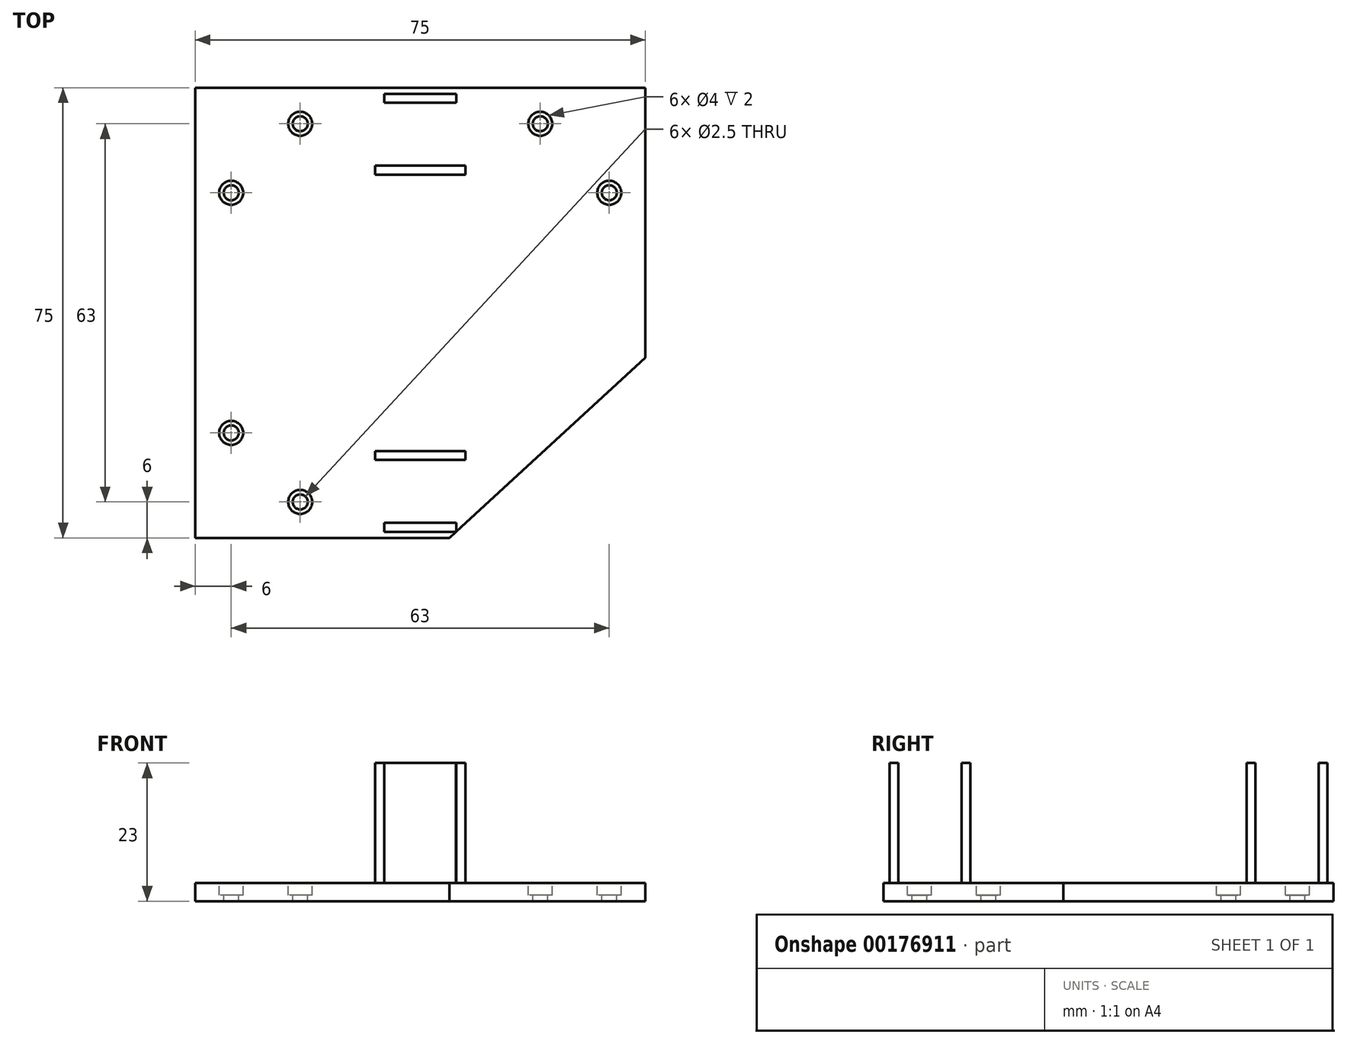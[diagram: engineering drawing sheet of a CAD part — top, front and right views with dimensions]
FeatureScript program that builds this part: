
annotation { "Feature Type Name" : "Feature", "Feature Type Description" : "" }
export const myFeature = defineFeature(function(context is Context, id is Id, definition is map)
    precondition{}
    {
        {
            var Q0;
            Q0=qCreatedBy(makeId("Top.planeOp"),FACE);
            var sketch = newSketch(context, id + "F0", { "sketchPlane" : qUnion([Q0])});
            skLineSegment(sketch, "E0.bottom", {"start": v(-37.5, 37.5) * mm, "end": v(37.5, 37.5) * mm});
            skLineSegment(sketch, "E0.top", {"start": v(-37.5, -37.5) * mm, "end": v(37.5, -37.5) * mm});
            skLineSegment(sketch, "E0.left", {"start": v(-37.5, 37.5) * mm, "end": v(-37.5, -37.5) * mm});
            skLineSegment(sketch, "E0.right", {"start": v(37.5, 37.5) * mm, "end": v(37.5, -37.5) * mm});
            skSolve(sketch);
        }
        {
            var Q0;
            Q0=makeQuery(id+"F0.imprint","IMPRINT",FACE,{"disambiguationData":[TD([[makeQuery(id+"F0.imprint","IMPRINT",EDGE,{"derivedFrom":sQuery(id+"F0.wireOp",EDGE,"E0.bottom")}),-1.0]])]});
            extrude(context, id + "F1", {"entities" : qUnion([Q0]), "depth" : 3 * mm});
        }
        {
            var Q0;
            Q0=makeQuery(id+"F1.opExtrude","CAP_FACE",FACE,{"disambiguationData":[OSD([sQuery(id+"F0.wireOp",EDGE,"E0.bottom"),sQuery(id+"F0.wireOp",EDGE,"E0.top"),sQuery(id+"F0.wireOp",EDGE,"E0.left"),sQuery(id+"F0.wireOp",EDGE,"E0.right")])],"isStart":false});
            var sketch = newSketch(context, id + "F2", { "sketchPlane" : qUnion([Q0])});
            skCircle(sketch, "E1", {"center": v(31.5, -20) * mm, "radius": 2 * mm});
            skCircle(sketch, "E2", {"center": v(20, -31.5) * mm, "radius": 2 * mm});
            skCircle(sketch, "E3", {"center": v(31.5, 20) * mm, "radius": 2 * mm});
            skCircle(sketch, "E4", {"center": v(20, 31.5) * mm, "radius": 2 * mm});
            skCircle(sketch, "E5", {"center": v(-20, 31.5) * mm, "radius": 2 * mm});
            skCircle(sketch, "E6", {"center": v(-31.5, 20) * mm, "radius": 2 * mm});
            skCircle(sketch, "E7", {"center": v(-20, -31.5) * mm, "radius": 2 * mm});
            skCircle(sketch, "E8", {"center": v(-31.5, -20) * mm, "radius": 2 * mm});
            skSolve(sketch);
        }
        {
            var Q0;
            Q0 = qSketchRegion(id + "F2", true);
            extrude(context, id + "F3", {"entities" : qUnion([Q0]), "operationType" : NewBodyOperationType.REMOVE, "oppositeDirection" : true, "depth" : 2 * mm});
        }
        {
            var Q0;
            Q0=makeQuery(id+"F3.boolean.opBoolean","COPY",FACE,{"derivedFrom":makeQuery(id+"F3.opExtrude","CAP_FACE",FACE,{"disambiguationData":[OSD([sQuery(id+"F2.wireOp",EDGE,"E8")])],"isStart":false})});
            var sketch = newSketch(context, id + "F4", { "sketchPlane" : qUnion([Q0])});
            skCircle(sketch, "E9", {"center": v(-31.5, 20) * mm, "radius": 1.25 * mm});
            skCircle(sketch, "E10", {"center": v(-20, 31.5) * mm, "radius": 1.25 * mm});
            skCircle(sketch, "E11", {"center": v(20, 31.5) * mm, "radius": 1.25 * mm});
            skCircle(sketch, "E12", {"center": v(31.5, 20) * mm, "radius": 1.25 * mm});
            skCircle(sketch, "E13", {"center": v(-31.5, -20) * mm, "radius": 1.25 * mm});
            skCircle(sketch, "E14", {"center": v(31.5, -20) * mm, "radius": 1.25 * mm});
            skCircle(sketch, "E15", {"center": v(20, -31.5) * mm, "radius": 1.25 * mm});
            skCircle(sketch, "E16", {"center": v(-20, -31.5) * mm, "radius": 1.25 * mm});
            skSolve(sketch);
        }
        {
            var Q0;
            Q0 = qSketchRegion(id + "F4", true);
            extrude(context, id + "F5", {"entities" : qUnion([Q0]), "operationType" : NewBodyOperationType.REMOVE, "endBound" : BoundingType.THROUGH_ALL, "oppositeDirection" : true, "depth" : 25 * mm});
        }
        {
            var Q0;
            Q0=makeQuery(id+"F1.opExtrude","CAP_FACE",FACE,{"disambiguationData":[OSD([sQuery(id+"F0.wireOp",EDGE,"E0.bottom"),sQuery(id+"F0.wireOp",EDGE,"E0.top"),sQuery(id+"F0.wireOp",EDGE,"E0.left"),sQuery(id+"F0.wireOp",EDGE,"E0.right")])],"isStart":false});
            var sketch = newSketch(context, id + "F6", { "sketchPlane" : qUnion([Q0])});
            skLineSegment(sketch, "E17.bottom", {"start": v(-7.5, -23) * mm, "end": v(7.5, -23) * mm});
            skLineSegment(sketch, "E17.top", {"start": v(-7.5, -24.5) * mm, "end": v(7.5, -24.5) * mm});
            skLineSegment(sketch, "E17.left", {"start": v(-7.5, -23) * mm, "end": v(-7.5, -24.5) * mm});
            skLineSegment(sketch, "E17.right", {"start": v(7.5, -23) * mm, "end": v(7.5, -24.5) * mm});
            skLineSegment(sketch, "E18.bottom", {"start": v(-7.5, 23) * mm, "end": v(7.5, 23) * mm});
            skLineSegment(sketch, "E18.top", {"start": v(-7.5, 24.5) * mm, "end": v(7.5, 24.5) * mm});
            skLineSegment(sketch, "E18.left", {"start": v(-7.5, 23) * mm, "end": v(-7.5, 24.5) * mm});
            skLineSegment(sketch, "E18.right", {"start": v(7.5, 23) * mm, "end": v(7.5, 24.5) * mm});
            skSolve(sketch);
        }
        {
            var Q0;
            Q0 = qSketchRegion(id + "F6", true);
            extrude(context, id + "F7", {"entities" : qUnion([Q0]), "operationType" : NewBodyOperationType.ADD, "depth" : 20 * mm});
        }
        {
            var Q0;
            Q0=makeQuery(id+"F1.opExtrude","CAP_FACE",FACE,{"disambiguationData":[OSD([sQuery(id+"F0.wireOp",EDGE,"E0.bottom"),sQuery(id+"F0.wireOp",EDGE,"E0.top"),sQuery(id+"F0.wireOp",EDGE,"E0.left"),sQuery(id+"F0.wireOp",EDGE,"E0.right")])],"isStart":false});
            var sketch = newSketch(context, id + "F8", { "sketchPlane" : qUnion([Q0])});
            skLineSegment(sketch, "E19.bottom", {"start": v(-6, -36.5) * mm, "end": v(6, -36.5) * mm});
            skLineSegment(sketch, "E19.top", {"start": v(-6, -35) * mm, "end": v(6, -35) * mm});
            skLineSegment(sketch, "E19.left", {"start": v(-6, -36.5) * mm, "end": v(-6, -35) * mm});
            skLineSegment(sketch, "E19.right", {"start": v(6, -36.5) * mm, "end": v(6, -35) * mm});
            skLineSegment(sketch, "E20.bottom", {"start": v(-6, 35) * mm, "end": v(6, 35) * mm});
            skLineSegment(sketch, "E20.top", {"start": v(-6, 36.5) * mm, "end": v(6, 36.5) * mm});
            skLineSegment(sketch, "E20.left", {"start": v(-6, 35) * mm, "end": v(-6, 36.5) * mm});
            skLineSegment(sketch, "E20.right", {"start": v(6, 35) * mm, "end": v(6, 36.5) * mm});
            skSolve(sketch);
        }
        {
            var Q0;
            Q0 = qSketchRegion(id + "F8", true);
            extrude(context, id + "F9", {"entities" : qUnion([Q0]), "operationType" : NewBodyOperationType.ADD, "depth" : 20 * mm});
        }
        {
            var Q0;
            Q0=makeQuery(id+"F1.opExtrude","CAP_FACE",FACE,{"disambiguationData":[OSD([sQuery(id+"F0.wireOp",EDGE,"E0.bottom"),sQuery(id+"F0.wireOp",EDGE,"E0.top"),sQuery(id+"F0.wireOp",EDGE,"E0.left"),sQuery(id+"F0.wireOp",EDGE,"E0.right")])],"isStart":true});
            var sketch = newSketch(context, id + "F10", { "sketchPlane" : qUnion([Q0])});
            skLineSegment(sketch, "E21", {"start": v(4.86, 37.5) * mm, "end": v(37.5, 37.5) * mm});
            skLineSegment(sketch, "E22", {"start": v(37.5, 37.5) * mm, "end": v(37.5, 7.5) * mm});
            skLineSegment(sketch, "E23", {"start": v(37.5, 7.5) * mm, "end": v(4.86, 37.5) * mm});
            skSolve(sketch);
        }
        {
            var Q0;
            Q0 = qSketchRegion(id + "F10", true);
            var Q1;
            Q1=makeQuery(id+"F10.imprint","IMPRINT",FACE,{"disambiguationData":[TD([[makeQuery(id+"F10.imprint","IMPRINT",EDGE,{"derivedFrom":sQuery(id+"F10.wireOp",EDGE,"E21")}),-1.0]])]});
            extrude(context, id + "F11", {"entities" : qUnion([Q0, Q1]), "operationType" : NewBodyOperationType.REMOVE, "endBound" : BoundingType.THROUGH_ALL, "oppositeDirection" : true, "depth" : 25 * mm});
        }
    });
